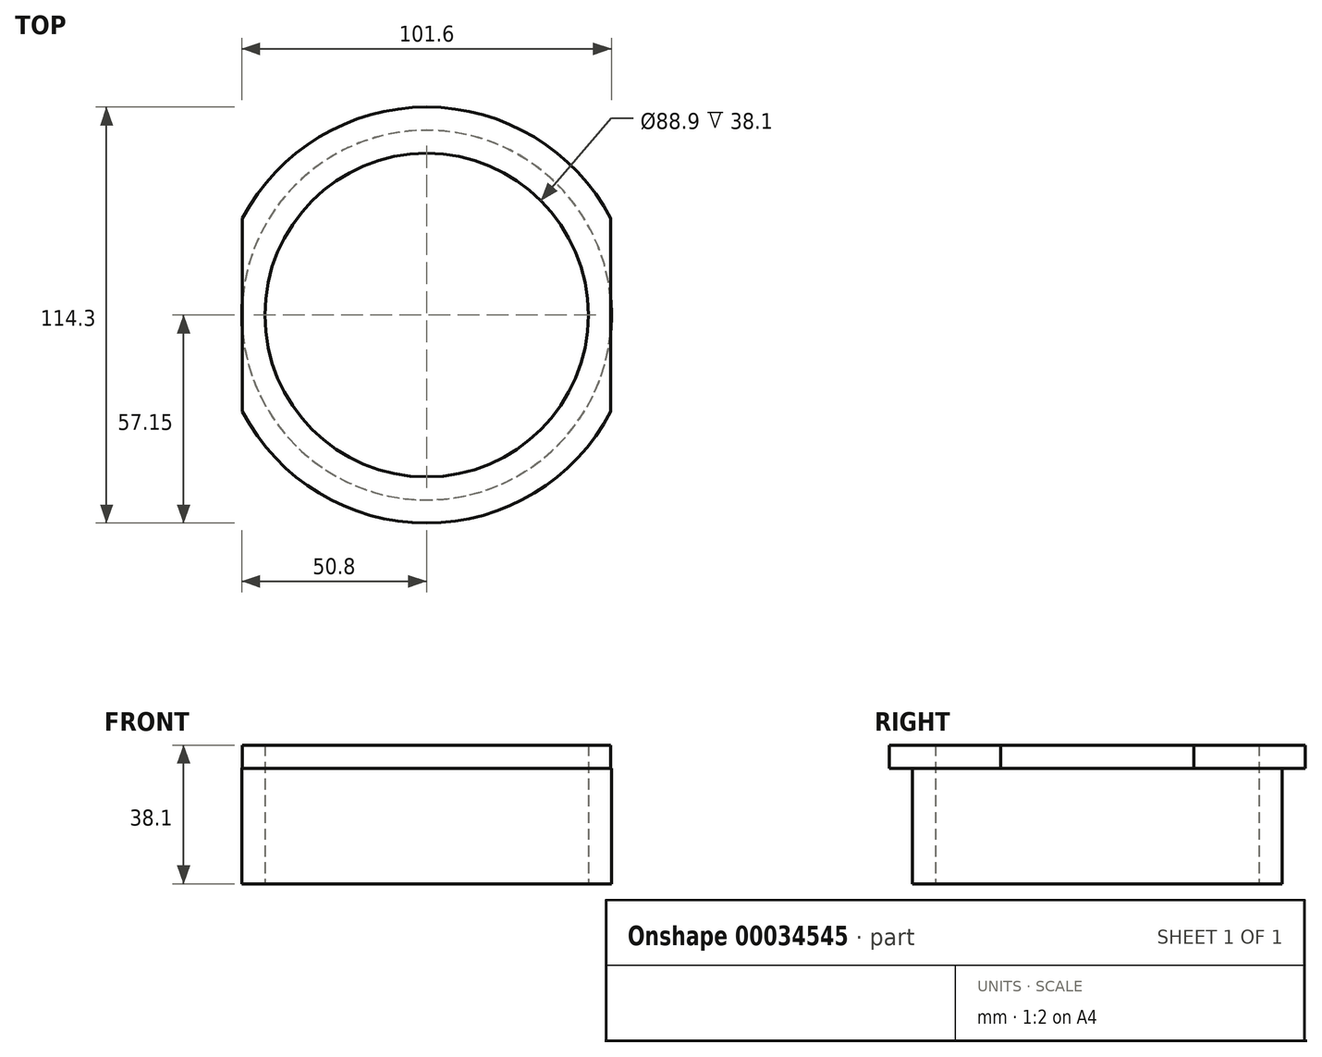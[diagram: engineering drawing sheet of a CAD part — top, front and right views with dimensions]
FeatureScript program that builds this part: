
annotation { "Feature Type Name" : "Feature", "Feature Type Description" : "" }
export const myFeature = defineFeature(function(context is Context, id is Id, definition is map)
    precondition{}
    {
        {
            var Q0;
            Q0=qCreatedBy(makeId("Top.planeOp"),FACE);
            var sketch = newSketch(context, id + "F0", { "sketchPlane" : qUnion([Q0])});
            skCircle(sketch, "E0", {"center": v(0, 0) * mm, "radius": 50.8 * mm});
            skCircle(sketch, "E1.0", {"center": v(0, 0) * mm, "radius": 44.45 * mm});
            skSolve(sketch);
        }
        {
            var Q0;
            Q0=makeQuery(id+"F0.imprint","IMPRINT",FACE,{"disambiguationData":[TD([[makeQuery(id+"F0.imprint","IMPRINT",EDGE,{"derivedFrom":sQuery(id+"F0.wireOp",EDGE,"E0")}),1.0]])]});
            extrude(context, id + "F1", {"entities" : qUnion([Q0]), "depth" : 31.75 * mm});
        }
        {
            var Q0;
            Q0=makeQuery(id+"F1.opExtrude","CAP_FACE",FACE,{"disambiguationData":[OSD([sQuery(id+"F0.wireOp",EDGE,"E0"),sQuery(id+"F0.wireOp",EDGE,"E1.0")])],"isStart":false});
            var sketch = newSketch(context, id + "F2", { "sketchPlane" : qUnion([Q0])});
            skArc(sketch, "E2.0", {"start": v(-50.61, -26.54) * mm, "mid": v(0, -57.15) * mm, "end": v(50.61, -26.54) * mm});
            skArc(sketch, "E3.trimOffspring", {"start": v(50.61, 26.54) * mm, "mid": v(0, 57.15) * mm, "end": v(-50.61, 26.54) * mm});
            skLineSegment(sketch, "E4.0", {"start": v(50.61, -26.54) * mm, "end": v(50.61, 26.54) * mm});
            skLineSegment(sketch, "E5.0", {"start": v(-50.61, -1.07) * mm, "end": v(-50.61, -26.54) * mm});
            skLineSegment(sketch, "E5.1", {"start": v(-50.61, -1.07) * mm, "end": v(-50.61, 26.54) * mm});
            skSolve(sketch);
        }
        {
            var Q0;
            Q0=qSketchRegion(id+"F2",true);
            extrude(context, id + "F3", {"entities" : qUnion([Q0]), "operationType" : NewBodyOperationType.ADD, "depth" : 6.35 * mm});
        }
        {
            var Q0;
            Q0=makeQuery(id+"F3.boolean.opBoolean","SPLIT",FACE,{"disambiguationData":[TD([makeQuery(id+"F1.opExtrude","SWEPT_FACE",FACE,{"disambiguationData":[OSD([sQuery(id+"F0.wireOp",EDGE,"E1.0")])]})])],"derivedFrom":makeQuery(id+"F3.opExtrude","CAP_FACE",FACE,{"disambiguationData":[OSD([sQuery(id+"F2.wireOp",EDGE,"E2.0"),sQuery(id+"F2.wireOp",EDGE,"ef11bcc9-c215-4255-b367-998e49c748a7.0"),sQuery(id+"F2.wireOp",EDGE,"ef11bcc9-c215-4255-b367-998e49c748a7.1"),sQuery(id+"F2.wireOp",EDGE,"301642ca-1711-41eb-a73b-8d7c0db3094d.0"),sQuery(id+"F2.wireOp",EDGE,"E3.trimOffspring")])],"isStart":true})});
            var sketch = newSketch(context, id + "F4", { "sketchPlane" : qUnion([Q0])});
            skCircle(sketch, "E6.0", {"center": v(0, 0) * mm, "radius": 44.45 * mm});
            skSolve(sketch);
        }
        {
            var Q0;
            Q0=makeQuery(id+"F4.imprint","IMPRINT",FACE,{"disambiguationData":[TD([[makeQuery(id+"F4.imprint","IMPRINT",EDGE,{"derivedFrom":sQuery(id+"F4.wireOp",EDGE,"E6.0")}),-1.0]])]});
            var Q1;
            Q1=sQuery(id+"F4.wireOp",EDGE,"E6.0");
            extrude(context, id + "F5", {"entities" : qUnion([Q0]), "operationType" : NewBodyOperationType.REMOVE, "surfaceEntities" : qUnion([Q1]), "oppositeDirection" : true, "depth" : 25.4 * mm});
        }
    });
